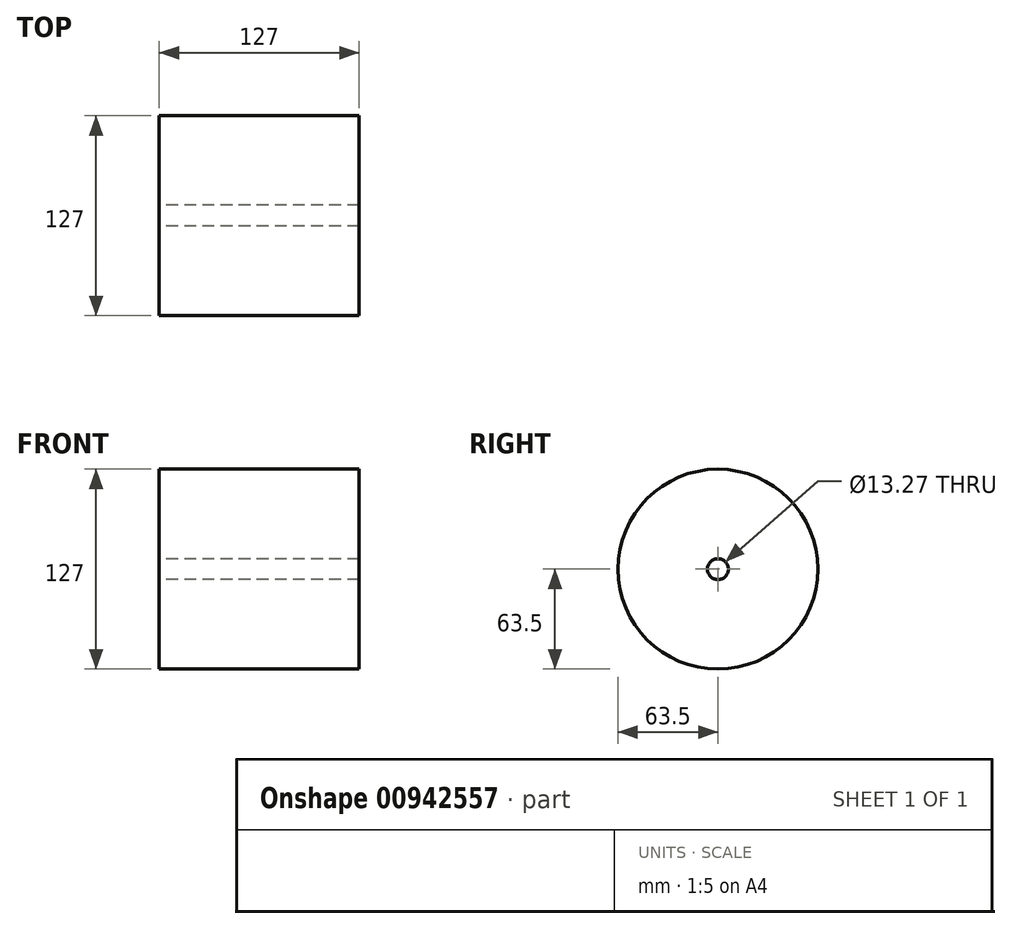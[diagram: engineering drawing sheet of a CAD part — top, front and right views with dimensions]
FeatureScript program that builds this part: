
annotation { "Feature Type Name" : "Feature", "Feature Type Description" : "" }
export const myFeature = defineFeature(function(context is Context, id is Id, definition is map)
    precondition{}
    {
        {
            var Q0;
            Q0=qCreatedBy(makeId("Right.planeOp"),FACE);
            var sketch = newSketch(context, id + "F0", { "sketchPlane" : qUnion([Q0])});
            skCircle(sketch, "E0", {"center": v(0, 0) * mm, "radius": 63.5 * mm});
            skCircle(sketch, "E1", {"center": v(0, 0) * mm, "radius": 6.63 * mm});
            skSolve(sketch);
        }
        {
            var Q0;
            Q0 = qSketchRegion(id + "F0", true);
            extrude(context, id + "F1", {"entities" : qUnion([Q0]), "depth" : 127 * mm, "offsetDistance" : 25.4 * mm});
        }
    });
